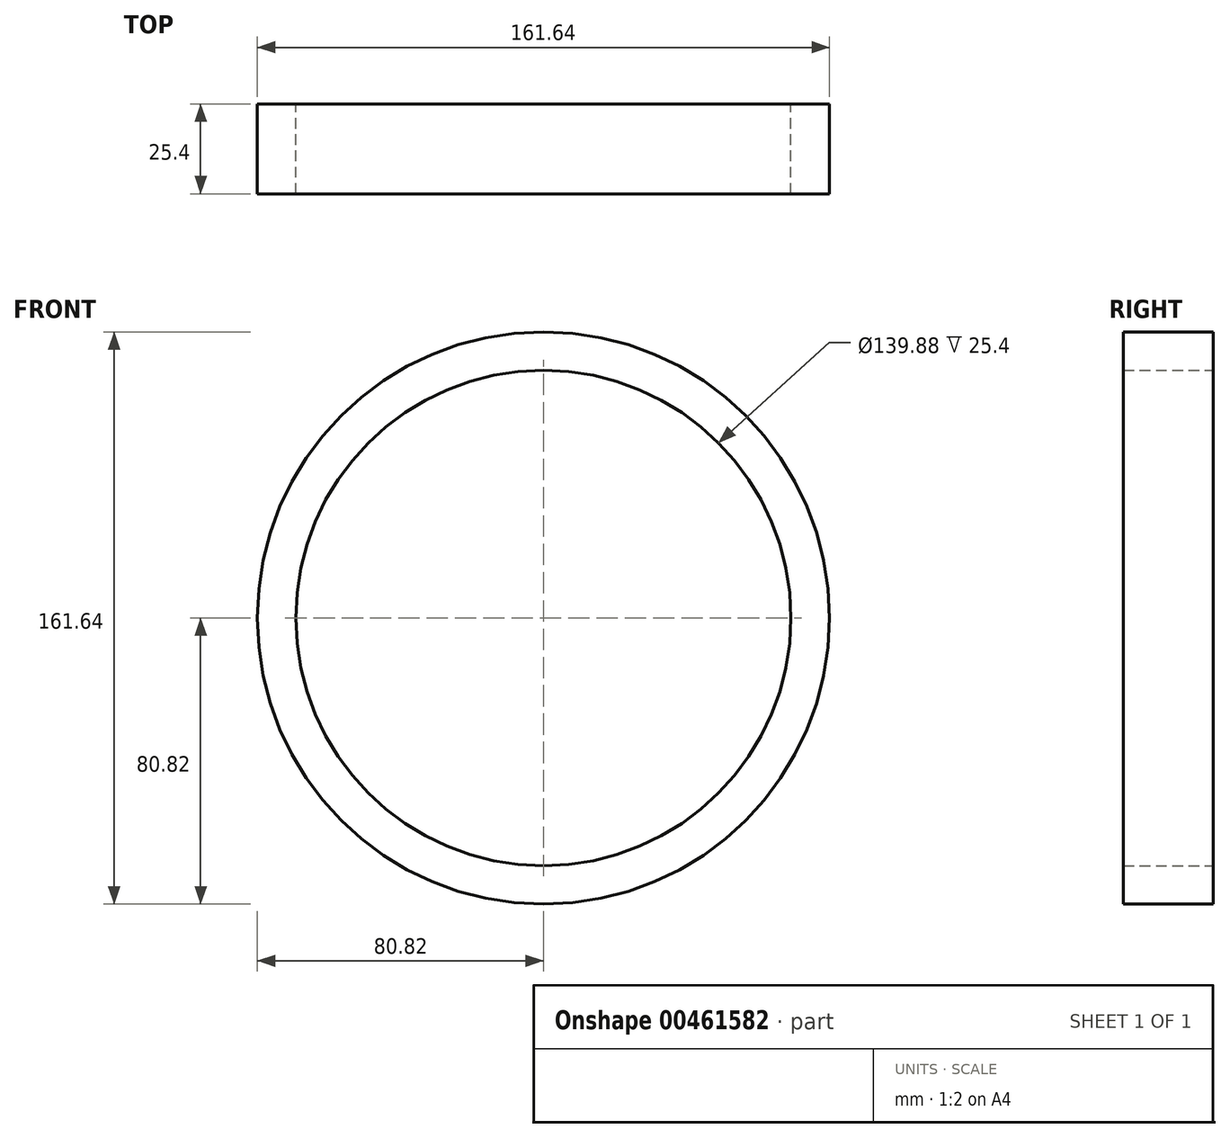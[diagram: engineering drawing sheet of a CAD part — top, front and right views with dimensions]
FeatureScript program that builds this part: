
annotation { "Feature Type Name" : "Feature", "Feature Type Description" : "" }
export const myFeature = defineFeature(function(context is Context, id is Id, definition is map)
    precondition{}
    {
        {
            var Q0;
            Q0=qCreatedBy(makeId("Front.planeOp"),FACE);
            var sketch = newSketch(context, id + "F0", { "sketchPlane" : qUnion([Q0])});
            skCircle(sketch, "E0", {"center": v(0, 0) * mm, "radius": 80.82 * mm});
            skCircle(sketch, "E1", {"center": v(0, 0) * mm, "radius": 69.94 * mm});
            skSolve(sketch);
        }
        {
            var Q0;
            Q0=makeQuery(id+"F0.imprint","IMPRINT",FACE,{"disambiguationData":[TD([[makeQuery(id+"F0.imprint","IMPRINT",EDGE,{"derivedFrom":sQuery(id+"F0.wireOp",EDGE,"E0")}),1.0]])]});
            extrude(context, id + "F1", {"entities" : qUnion([Q0]), "depth" : 25.4 * mm});
        }
    });
